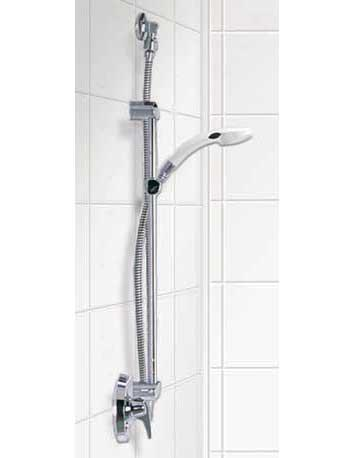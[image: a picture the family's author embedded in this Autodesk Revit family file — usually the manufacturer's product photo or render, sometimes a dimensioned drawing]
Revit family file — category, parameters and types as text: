
# Revit family: 14836FHA
name_source: partatom
category: Plumbing Fixtures
revit_build: Autodesk Revit 2018 (Build: 20190510_1515(x64)
units: mm (PartAtom-declared; Revit-internal decimal feet)

## family parameters
Always vertical = Yes
Cut with Voids When Loaded = No
OmniClass Number = 23.45.00.00
OmniClass Title = Sanitary, Laundry, and Cleaning Equipment
Part Type = Normal
Room Calculation Point = No
Round Connector Dimension = Use Diameter
Shared = No
Work Plane-Based = No

## types (2) — shared parameters
Assembly Code = D2010710
Drain = 3 1/4"
Grab Bars = Steel-Comfort Designs Bathware-304-Stainless Steel
Keynote = COMPRESSION-MOLDED  SOLID  SURFACE  SHOWER  BASE W/ TRENCH DRAIN
Manufacturer = Comfort Designs
MasterFormat Number = 22.42.23
MasterFormat Title = Commercial Showers
Nailing Flange = 1"
OmniClass Number = 23.45.05.14.11.21
OmniClass Title = Shower Receptors
S Bar Level = 34 5/8"
Seat Finish = Steel-Comfort Designs Bathware-304-Stainless Steel
Seat Level = 18 5/8"
Smooth Gelcoat = Gelcoat-Asura-White
Trench drain material = Drain
URL = http://www.comfortdesignsbathware.com

## per-type parameters (varying)
| type | Back Wall Thickness | Center of Shower | Depth | Description | Drain Offset Side | Drain Offset Wall | Height | Length | Part Thickness | Side Wall Thickness |
| SWB3838TR.75 | 7/8" | 19" | 37" | 38"W x 37"D COMPRESSION-MOLDED  SOLID  SURFACE  SHOWER  BASE W/ TRENCH DRAIN | 19" | 33 1/2" | 2 1/2" | 38" | 1/8" | 7/8" |
| SWB6234TR.75 | 1 1/2" | 25 5/16" | 37 5/8" | 62"W x 33"D COMPRESSION-MOLDED  SOLID  SURFACE  SHOWER  BASE W/ TRENCH DRAIN | 25 5/16" | 19 1/4" | 78" | 50 5/8" | 1/4" | 1 1/2" |

note: column(s) folded — value = type name in every type: Model

## geometry (parser evidence)
native form markers: Blend x4, Sweep x24
no freeform markers — native parametric forms only
